# Revit family: HOMECARE LIN RAIL SHWR 900 STR BAR
name_source: partatom
category: Plumbing Fixtures
units: mm (PartAtom-declared; Revit-internal decimal feet)

## family parameters
Cut with Voids When Loaded = No
Host = Face
OmniClass Number = 23.45.05.14.17
OmniClass Title = Showers
Part Type = Normal
Room Calculation Point = No
Round Connector Dimension = Use Diameter
Shared = No

## types (3) — shared parameters
Assembly Code = D2020300
CW Connection = Yes
HW Connection = Yes
Manufacturer = GWA Bathrooms & Kitchens
Material_Sprays = GWA-Plastic-General
URL = https://www.caroma.com.au
Vent Connection = No
Waste Connection = No
zero-valued in all types: Default Elevation

## per-type parameters (varying)
| type | Material | Material_Face | Model |
| HOMECARE LIN RAIL SHWR 900 STR BAR PSS | GWA_Metal-Polished Stainless | GWA-Plastic-White | 98280PSS3A |
| HOMECARE LIN RAIL SHWR 900 STR BAR BLK | GWA-Metal-Black | GWA-Plastic-Black | 98280B3A |
| HOMECARE LIN RAIL SHWR 900 STR BAR BN | GWA_Metal-Brushed-Nickel | GWA-Plastic-White | 98280BN3A |

note: column(s) folded — value = type name in every type: Description

## geometry (parser evidence)
native form markers: Sweep x8
no freeform markers — native parametric forms only
